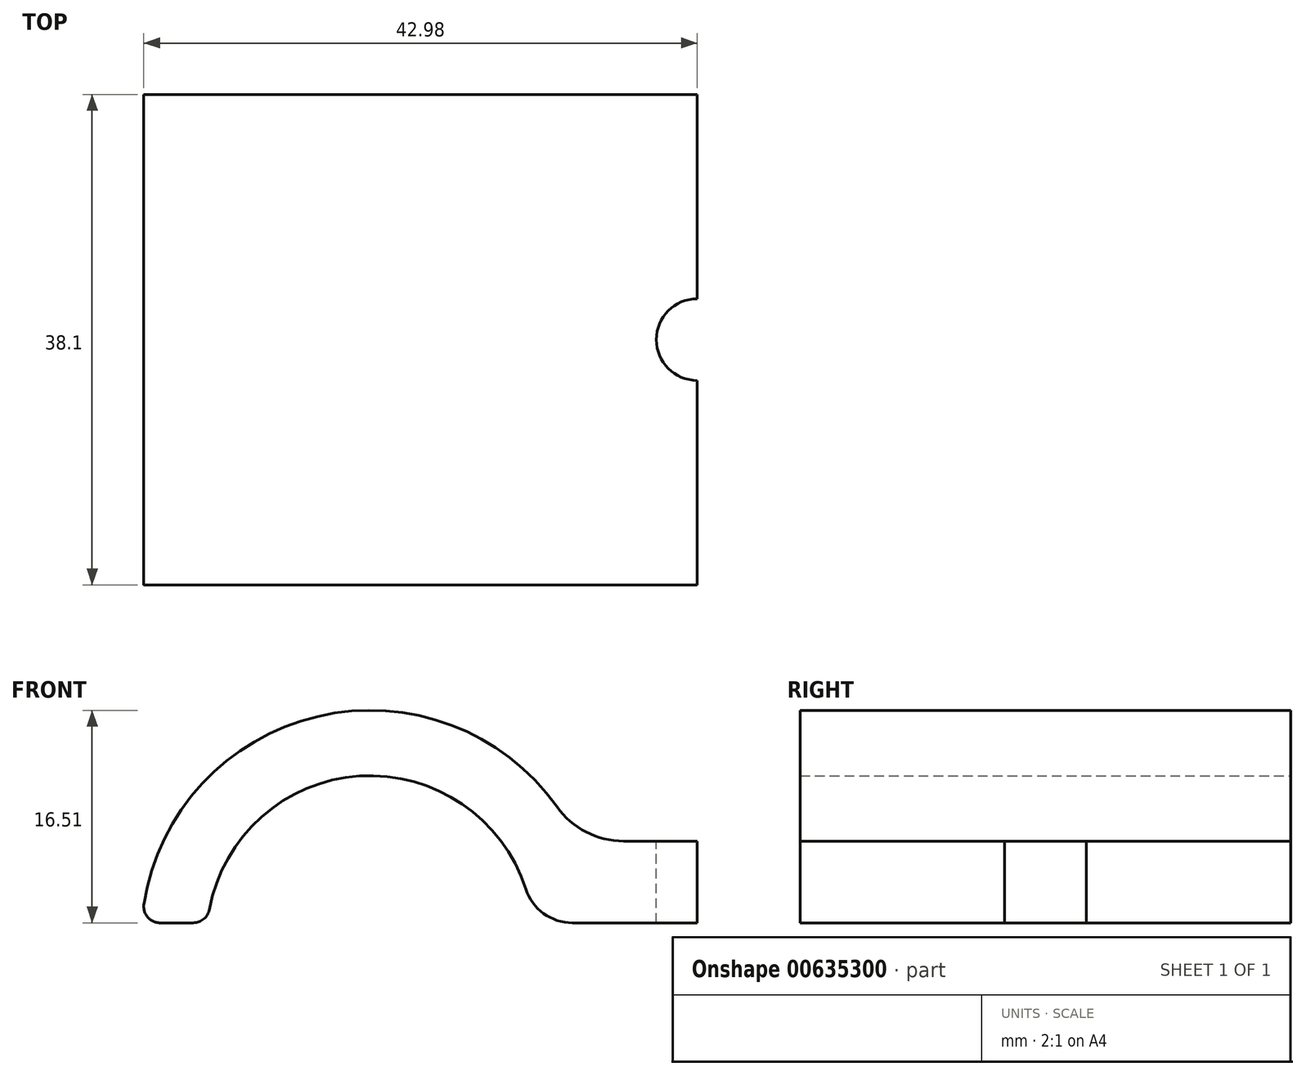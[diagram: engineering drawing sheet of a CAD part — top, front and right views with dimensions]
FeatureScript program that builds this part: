
annotation { "Feature Type Name" : "Feature", "Feature Type Description" : "" }
export const myFeature = defineFeature(function(context is Context, id is Id, definition is map)
    precondition{}
    {
        {
            var Q0;
            Q0=qCreatedBy(makeId("Front.planeOp"),FACE);
            var sketch = newSketch(context, id + "F0", { "sketchPlane" : qUnion([Q0])});
            skArc(sketch, "E0", {"start": v(12.08, 3.9) * mm, "mid": v(-0.82, 12.67) * mm, "end": v(-12.49, 2.3) * mm});
            skArc(sketch, "E1", {"start": v(14.5, 10.3) * mm, "mid": v(-4.08, 17.3) * mm, "end": v(-17.57, 2.74) * mm});
            skLineSegment(sketch, "E2", {"start": v(25.4, 17.49) * mm, "end": v(25.4, -32.66) * mm});
            skLineSegment(sketch, "E3.0", {"start": v(19.67, -7.62) * mm, "end": v(25.4, -7.62) * mm});
            skLineSegment(sketch, "E4.trimOffspring", {"start": v(19.67, 7.62) * mm, "end": v(25.4, 7.62) * mm});
            skPoint(sketch, "E5.visualSharp", {"position": v(16.06, 7.62) * mm});
            skArc(sketch, "E5.filletArc", {"start": v(14.5, 10.3) * mm, "mid": v(16.76, 8.33) * mm, "end": v(19.67, 7.62) * mm});
            skPoint(sketch, "E6.visualSharp", {"position": v(16.06, -7.62) * mm});
            skArc(sketch, "E6.filletArc", {"start": v(19.67, -7.62) * mm, "mid": v(16.76, -8.33) * mm, "end": v(14.5, -10.3) * mm});
            skArc(sketch, "E7.MirrorCS", {"start": v(36.3, 10.3) * mm, "mid": v(54.88, 17.3) * mm, "end": v(68.37, 2.74) * mm});
            skArc(sketch, "E8.MirrorC", {"start": v(38.72, 3.9) * mm, "mid": v(51.62, 12.67) * mm, "end": v(63.29, 2.3) * mm});
            skArc(sketch, "E9.MirrorCS", {"start": v(31.13, -7.62) * mm, "mid": v(34.04, -8.33) * mm, "end": v(36.3, -10.3) * mm});
            skArc(sketch, "E10.MirrorCS", {"start": v(36.3, 10.3) * mm, "mid": v(34.04, 8.33) * mm, "end": v(31.13, 7.62) * mm});
            skLineSegment(sketch, "E11.MirrorCS", {"start": v(31.13, 7.62) * mm, "end": v(25.4, 7.62) * mm});
            skLineSegment(sketch, "E12.MirrorCS", {"start": v(31.13, -7.62) * mm, "end": v(25.4, -7.62) * mm});
            skLineSegment(sketch, "E13.0", {"start": v(16.06, 0) * mm, "end": v(34.74, 0) * mm});
            skLineSegment(sketch, "E14.0", {"start": v(15.7, 1.27) * mm, "end": v(35.1, 1.27) * mm});
            skPoint(sketch, "E15.visualSharp", {"position": v(12.7, 0) * mm});
            skArc(sketch, "E15.filletArc", {"start": v(16.06, 0) * mm, "mid": v(13.7, -0.82) * mm, "end": v(12.36, -2.93) * mm});
            skPoint(sketch, "E16.visualSharp", {"position": v(12.64, 1.27) * mm});
            skArc(sketch, "E16.filletArc", {"start": v(12.08, 3.9) * mm, "mid": v(13.47, 2) * mm, "end": v(15.7, 1.27) * mm});
            skPoint(sketch, "E17.visualSharp", {"position": v(38.16, 1.27) * mm});
            skArc(sketch, "E17.filletArc", {"start": v(35.1, 1.27) * mm, "mid": v(37.33, 2) * mm, "end": v(38.72, 3.9) * mm});
            skPoint(sketch, "E18.visualSharp", {"position": v(38.1, 0) * mm});
            skArc(sketch, "E18.filletArc", {"start": v(38.44, -2.93) * mm, "mid": v(37.1, -0.82) * mm, "end": v(34.74, 0) * mm});
            skLineSegment(sketch, "E19", {"start": v(-13.74, 1.27) * mm, "end": v(-16.31, 1.27) * mm});
            skLineSegment(sketch, "E20", {"start": v(-13.91, 0) * mm, "end": v(-16.46, 0) * mm});
            skArc(sketch, "E21.trimOffspring", {"start": v(-17.73, -1.37) * mm, "mid": v(-4.75, -17.13) * mm, "end": v(14.5, -10.3) * mm});
            skArc(sketch, "E22.trimOffspring", {"start": v(-12.65, -1.15) * mm, "mid": v(-0.9, -12.67) * mm, "end": v(12.36, -2.93) * mm});
            skPoint(sketch, "E23.visualSharp", {"position": v(-17.73, 1.27) * mm});
            skArc(sketch, "E23.filletArc", {"start": v(-17.57, 2.74) * mm, "mid": v(-17.28, 1.71) * mm, "end": v(-16.31, 1.27) * mm});
            skPoint(sketch, "E24.visualSharp", {"position": v(-12.64, 1.27) * mm});
            skArc(sketch, "E24.filletArc", {"start": v(-13.74, 1.27) * mm, "mid": v(-12.92, 1.56) * mm, "end": v(-12.49, 2.3) * mm});
            skPoint(sketch, "E25.visualSharp", {"position": v(-12.7, 0) * mm});
            skArc(sketch, "E25.filletArc", {"start": v(-12.65, -1.15) * mm, "mid": v(-13.06, -0.33) * mm, "end": v(-13.91, 0) * mm});
            skPoint(sketch, "E26.visualSharp", {"position": v(-17.78, 0) * mm});
            skArc(sketch, "E26.filletArc", {"start": v(-16.46, 0) * mm, "mid": v(-17.4, -0.4) * mm, "end": v(-17.73, -1.37) * mm});
            skLineSegment(sketch, "E27", {"start": v(64.54, 1.27) * mm, "end": v(67.11, 1.27) * mm});
            skLineSegment(sketch, "E28", {"start": v(64.71, 0) * mm, "end": v(67.26, 0) * mm});
            skArc(sketch, "E29.trimOffspring", {"start": v(63.45, -1.15) * mm, "mid": v(51.7, -12.67) * mm, "end": v(38.44, -2.93) * mm});
            skArc(sketch, "E30.trimOffspring", {"start": v(68.53, -1.37) * mm, "mid": v(55.55, -17.13) * mm, "end": v(36.3, -10.3) * mm});
            skPoint(sketch, "E31.visualSharp", {"position": v(63.44, 1.27) * mm});
            skArc(sketch, "E31.filletArc", {"start": v(63.29, 2.3) * mm, "mid": v(63.72, 1.56) * mm, "end": v(64.54, 1.27) * mm});
            skPoint(sketch, "E32.visualSharp", {"position": v(68.53, 1.27) * mm});
            skArc(sketch, "E32.filletArc", {"start": v(67.11, 1.27) * mm, "mid": v(68.08, 1.71) * mm, "end": v(68.37, 2.74) * mm});
            skPoint(sketch, "E33.visualSharp", {"position": v(68.58, 0) * mm});
            skArc(sketch, "E33.filletArc", {"start": v(68.53, -1.37) * mm, "mid": v(68.2, -0.4) * mm, "end": v(67.26, 0) * mm});
            skPoint(sketch, "E34.visualSharp", {"position": v(63.5, 0) * mm});
            skArc(sketch, "E34.filletArc", {"start": v(64.71, 0) * mm, "mid": v(63.86, -0.33) * mm, "end": v(63.45, -1.15) * mm});
            skSolve(sketch);
        }
        {
            var Q0;
            Q0=makeQuery(id+"F0.imprint","IMPRINT",FACE,{"disambiguationData":[TD([[makeQuery(id+"F0.imprint","IMPRINT",EDGE,{"derivedFrom":sQuery(id+"F0.wireOp",EDGE,"E7.MirrorCS")}),-1.0]])]});
            var Q1;
            Q1=makeQuery(id+"F0.imprint","IMPRINT",FACE,{"disambiguationData":[TD([[makeQuery(id+"F0.imprint","IMPRINT",EDGE,{"derivedFrom":sQuery(id+"F0.wireOp",EDGE,"E0")}),-1.0]])]});
            extrude(context, id + "F1", {"entities" : qUnion([Q0, Q1]), "depth" : 38.1 * mm, "offsetDistance" : 25.4 * mm});
        }
        {
            var Q0;
            Q0=makeQuery(id+"F1.opExtrude","SWEPT_FACE",FACE,{"disambiguationData":[OSD([sQuery(id+"F0.wireOp",EDGE,"E4.trimOffspring"),sQuery(id+"F0.wireOp",EDGE,"E11.MirrorCS")])]});
            var sketch = newSketch(context, id + "F2", { "sketchPlane" : qUnion([Q0])});
            skLineSegment(sketch, "E35", {"start": v(19.67, -19.05) * mm, "end": v(31.13, -19.05) * mm});
            skPoint(sketch, "E36.endSnap0", {"position": v(25.4, -19.05) * mm});
            skCircle(sketch, "E37", {"center": v(25.4, -19.05) * mm, "radius": 3.18 * mm});
            skSolve(sketch);
        }
        {
            var Q0;
            Q0=sQuery(id+"F2.wireOp",VERTEX,"E36.endSnap0");
            var Q1;
            Q1=makeQuery(id+"F1.opExtrude","SWEPT_BODY",BODY,{"disambiguationData":[OSD([sQuery(id+"F0.wireOp",EDGE,"E0"),sQuery(id+"F0.wireOp",EDGE,"E1"),sQuery(id+"F0.wireOp",EDGE,"E3.0"),sQuery(id+"F0.wireOp",EDGE,"E4.trimOffspring"),sQuery(id+"F0.wireOp",EDGE,"E5.filletArc"),sQuery(id+"F0.wireOp",EDGE,"E6.filletArc"),sQuery(id+"F0.wireOp",EDGE,"E7.MirrorCS"),sQuery(id+"F0.wireOp",EDGE,"E8.MirrorC"),sQuery(id+"F0.wireOp",EDGE,"E9.MirrorCS"),sQuery(id+"F0.wireOp",EDGE,"E10.MirrorCS"),sQuery(id+"F0.wireOp",EDGE,"E11.MirrorCS"),sQuery(id+"F0.wireOp",EDGE,"E12.MirrorCS"),sQuery(id+"F0.wireOp",EDGE,"E13.0"),sQuery(id+"F0.wireOp",EDGE,"E14.0"),sQuery(id+"F0.wireOp",EDGE,"E15.filletArc"),sQuery(id+"F0.wireOp",EDGE,"E16.filletArc"),sQuery(id+"F0.wireOp",EDGE,"E17.filletArc"),sQuery(id+"F0.wireOp",EDGE,"E18.filletArc")])]});
            hole(context, id + "F3", {"style" : HoleStyle.SIMPLE, "endStyle" : HoleEndStyle.THROUGH, "holeDiameter" : 6.35 * mm, "majorDiameter" : 6.35 * mm, "isTappedThrough" : true, "tappedDepth" : 12.7 * mm, "tapClearance" : 3, "locations" : qUnion([Q0]), "scope" : qUnion([Q1])});
        }
    });
